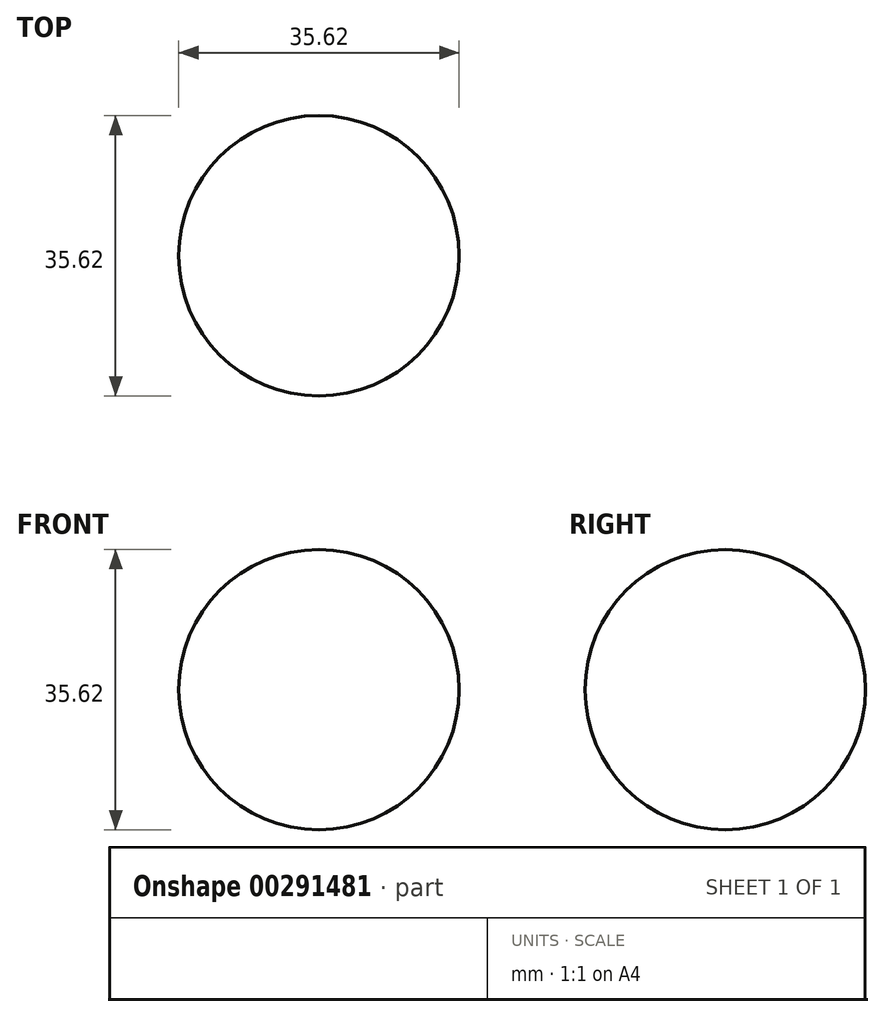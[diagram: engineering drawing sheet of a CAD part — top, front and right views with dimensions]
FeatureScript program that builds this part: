
annotation { "Feature Type Name" : "Feature", "Feature Type Description" : "" }
export const myFeature = defineFeature(function(context is Context, id is Id, definition is map)
    precondition{}
    {
        {
            var Q0;
            Q0=qCreatedBy(makeId("Top.planeOp"),FACE);
            var sketch = newSketch(context, id + "F0", { "sketchPlane" : qUnion([Q0])});
            skCircle(sketch, "E0", {"center": v(-50.23, 38.8) * mm, "radius": 17.8 * mm});
            skLineSegment(sketch, "E1", {"start": v(-50.23, 38.8) * mm, "end": v(-32.42, 38.8) * mm});
            skLineSegment(sketch, "E2", {"start": v(-50.23, 38.8) * mm, "end": v(-68.04, 38.8) * mm});
            skSolve(sketch);
        }
        {
            var Q0;
            {var subQ0=sQuery(id+"F0.wireOp",EDGE,"E1");Q0=makeQuery(id+"F0.imprint","IMPRINT",FACE,{"disambiguationData":[TD([[makeQuery(id+"F0.imprint","IMPRINT",EDGE,{"derivedFrom":subQ0}),1.0]])]});}
            var Q1;
            Q1=sQuery(id+"F0.wireOp",EDGE,"E2");
            revolve(context, id + "F1", {"entities" : qUnion([Q0]), "axis" : qUnion([Q1]), "revolveType" : RevolveType.FULL});
        }
    });
